FCSTD DOCUMENT  (FreeCAD 0.19R19405 (Git))
Label: Mid_Layer-Tent
License: All rights reserved
LicenseURL: http://en.wikipedia.org/wiki/All_rights_reserved
objects: Sketcher::SketchObject×1
note: 1 computed .brp shape members not serialized (recipe doc carries the construction recipe); baked Part::Feature solids carry a one-line shape summary decoded from their .brp

FEATURE [Sketcher::SketchObject] Sketch016
  sketch-geometry (51):
    g0: Circle CenterX=80.788 CenterY=-116.401 CenterZ=0 NormalX=0 NormalY=0 NormalZ=1 AngleXU=0 Radius=1.75
    g1: Circle CenterX=20.7203 CenterY=-116.401 CenterZ=0 NormalX=0 NormalY=0 NormalZ=1 AngleXU=0 Radius=1.75
    g2: Circle CenterX=141.006 CenterY=-116.404 CenterZ=0 NormalX=0 NormalY=0 NormalZ=1 AngleXU=0 Radius=1.75
    g3: Circle CenterX=150.401 CenterY=-95.6476 CenterZ=0 NormalX=0 NormalY=0 NormalZ=1 AngleXU=0 Radius=3.25
    g4: Circle CenterX=20.5561 CenterY=-65.7042 CenterZ=0 NormalX=0 NormalY=0 NormalZ=1 AngleXU=0 Radius=1.75
    g5: Circle CenterX=140.998 CenterY=-65.6964 CenterZ=0 NormalX=0 NormalY=0 NormalZ=1 AngleXU=0 Radius=1.75
    g6: Circle CenterX=150.401 CenterY=-35.6697 CenterZ=0 NormalX=0 NormalY=0 NormalZ=1 AngleXU=0 Radius=3.25
    g7: Circle CenterX=20.3207 CenterY=-14.9935 CenterZ=0 NormalX=0 NormalY=0 NormalZ=1 AngleXU=0 Radius=1.75
    g8: Circle CenterX=141.013 CenterY=-14.9255 CenterZ=0 NormalX=0 NormalY=0 NormalZ=1 AngleXU=0 Radius=1.75
    g9: Circle CenterX=79.4493 CenterY=-8.03912 CenterZ=0 NormalX=0 NormalY=0 NormalZ=1 AngleXU=0 Radius=1.75
    g10: Circle CenterX=105.449 CenterY=-8.03912 CenterZ=0 NormalX=0 NormalY=0 NormalZ=1 AngleXU=0 Radius=1.75
    g11: LineSegment StartX=34.3805 StartY=-12.0047 StartZ=0 EndX=20.5805 EndY=-12.0047 EndZ=0
    g12: LineSegment StartX=34.3805 StartY=-12.0047 StartZ=0 EndX=34.3805 EndY=-18.1547 EndZ=0
    g13: LineSegment StartX=17.3206 StartY=-15.0015 StartZ=0 EndX=17.3206 EndY=-23.1215 EndZ=0
    g14: LineSegment StartX=34.3805 StartY=-18.1547 StartZ=0 EndX=23.4606 EndY=-18.1547 EndZ=0
    g15: LineSegment StartX=23.4606 StartY=-18.1547 StartZ=0 EndX=23.4606 EndY=-113.255 EndZ=0
    g16: LineSegment StartX=17.3987 StartY=-48.1369 StartZ=0 EndX=17.3987 EndY=-82.9869 EndZ=0
    g17: LineSegment StartX=17.7203 StartY=-108.28 StartZ=0 EndX=17.7203 EndY=-116.42 EndZ=0
    g18: LineSegment StartX=20.7013 StartY=-119.401 StartZ=0 EndX=141.151 EndY=-119.401 EndZ=0
    g19: LineSegment StartX=137.861 StartY=-113.251 StartZ=0 EndX=23.711 EndY=-113.251 EndZ=0
    g20: LineSegment StartX=137.861 StartY=-113.251 StartZ=0 EndX=137.861 EndY=-18.151 EndZ=0
    g21: LineSegment StartX=138.084 StartY=-18.151 StartZ=0 EndX=127.164 EndY=-18.151 EndZ=0
    g22: LineSegment StartX=127.211 StartY=-11.999 StartZ=0 EndX=127.211 EndY=-18.149 EndZ=0
    g23: LineSegment StartX=140.999 StartY=-11.9255 StartZ=0 EndX=127.199 EndY=-11.9255 EndZ=0
    g24: ArcOfCircle CenterX=20.3207 CenterY=-14.9935 CenterZ=0 NormalX=0 NormalY=0 NormalZ=1 AngleXU=0 Radius=3.00006 StartAngle=1.48407 EndAngle=3.14425
    g25: ArcOfCircle CenterX=20.7203 CenterY=-116.401 CenterZ=0 NormalX=0 NormalY=0 NormalZ=1 AngleXU=0 Radius=3.00006 StartAngle=3.14791 EndAngle=4.70607
    g26: ArcOfCircle CenterX=141.006 CenterY=-116.404 CenterZ=0 NormalX=0 NormalY=0 NormalZ=1 AngleXU=0 Radius=3.00006 StartAngle=4.76072 EndAngle=6.28982
    g27: ArcOfCircle CenterX=11.3242 CenterY=-22.9139 CenterZ=0 NormalX=0 NormalY=0 NormalZ=1 AngleXU=0 Radius=6 StartAngle=4.71644 EndAngle=6.24858
    g28: ArcOfCircle CenterX=11.3615 CenterY=-35.5431 CenterZ=0 NormalX=0 NormalY=0 NormalZ=1 AngleXU=0 Radius=6.62923 StartAngle=1.57276 EndAngle=4.71435
    g29: ArcOfCircle CenterX=11.3988 CenterY=-48.1722 CenterZ=0 NormalX=0 NormalY=0 NormalZ=1 AngleXU=0 Radius=6 StartAngle=0.00589337 EndAngle=1.57485
    g30: ArcOfCircle CenterX=141.013 CenterY=-14.9255 CenterZ=0 NormalX=0 NormalY=0 NormalZ=1 AngleXU=0 Radius=3.00006 StartAngle=6.24933 EndAngle=7.85859
    g31: LineSegment StartX=144.01 StartY=-108.261 StartZ=0 EndX=144.01 EndY=-116.401 EndZ=0
    g32: LineSegment StartX=144.814 StartY=-83.1385 StartZ=0 EndX=144.814 EndY=-48.2885 EndZ=0
    g33: LineSegment StartX=144.012 StartY=-23.12 StartZ=0 EndX=144.012 EndY=-15 EndZ=0
    g34: Circle CenterX=11.5597 CenterY=-95.5807 CenterZ=0 NormalX=0 NormalY=0 NormalZ=1 AngleXU=0 Radius=3.25
    g35: Circle CenterX=11.3615 CenterY=-35.5431 CenterZ=0 NormalX=0 NormalY=0 NormalZ=1 AngleXU=0 Radius=3.25
    g36: LineSegment StartX=76.1977 StartY=-5.03912 StartZ=0 EndX=108.263 EndY=-5.03912 EndZ=0
    g37: LineSegment StartX=108.303 StartY=-11.0391 StartZ=0 EndX=76.2376 EndY=-11.0391 EndZ=0
    g38: LineSegment StartX=75.4493 StartY=-10.0943 StartZ=0 EndX=75.4493 EndY=-5.76363 EndZ=0
    g39: LineSegment StartX=109.449 StartY=-10.0255 StartZ=0 EndX=109.449 EndY=-5.69488 EndZ=0
    g40: ArcOfCircle CenterX=76.4173 CenterY=-6.01471 CenterZ=0 NormalX=0 NormalY=0 NormalZ=1 AngleXU=0 Radius=1 StartAngle=1.79221 EndAngle=2.8878
    g41: ArcOfCircle CenterX=76.4488 CenterY=-10.0617 CenterZ=0 NormalX=0 NormalY=0 NormalZ=1 AngleXU=0 Radius=1 StartAngle=3.17423 EndAngle=4.4996
    g42: ArcOfCircle CenterX=108.5 CenterY=-6.01046 CenterZ=0 NormalX=0 NormalY=0 NormalZ=1 AngleXU=0 Radius=1 StartAngle=0.321062 EndAngle=1.81081
    g43: ArcOfCircle CenterX=108.45 CenterY=-10.05 CenterZ=0 NormalX=0 NormalY=0 NormalZ=1 AngleXU=0 Radius=1 StartAngle=4.56487 EndAngle=6.30762
    g44: ArcOfCircle CenterX=11.3988 CenterY=-82.9522 CenterZ=0 NormalX=0 NormalY=0 NormalZ=1 AngleXU=0 Radius=6 StartAngle=4.74889 EndAngle=6.27741
    g45: ArcOfCircle CenterX=11.5597 CenterY=-95.5807 CenterZ=0 NormalX=0 NormalY=0 NormalZ=1 AngleXU=0 Radius=6.63272 StartAngle=1.56205 EndAngle=4.70364
    g46: ArcOfCircle CenterX=11.7207 CenterY=-108.209 CenterZ=0 NormalX=0 NormalY=0 NormalZ=1 AngleXU=0 Radius=6 StartAngle=6.27138 EndAngle=7.89048
    g47: ArcOfCircle CenterX=150 CenterY=-22.9967 CenterZ=0 NormalX=0 NormalY=0 NormalZ=1 AngleXU=0 Radius=5.98868 StartAngle=3.16219 EndAngle=4.74658
    g48: ArcOfCircle CenterX=150.401 CenterY=-35.6697 CenterZ=0 NormalX=0 NormalY=0 NormalZ=1 AngleXU=0 Radius=6.69074 StartAngle=4.74177 EndAngle=7.88336
    g49: ArcOfCircle CenterX=150.802 CenterY=-48.3428 CenterZ=0 NormalX=0 NormalY=0 NormalZ=1 AngleXU=0 Radius=5.98868 StartAngle=1.60498 EndAngle=3.13253
    g50: LineSegment [constr] StartX=17.3987 StartY=-65.5619 StartZ=0 EndX=11.4606 EndY=-65.5619 EndZ=0
  constraints (113):
    c: DistanceX(g11,g11) = 13.8
    c: DistanceY(g12,g12) = 6.15
    c: DistanceY(g15,g15) = 95.1
    c: DistanceY(g13,g13) = 8.12
    c: DistanceY(g16,g16) = 34.85
    c: DistanceY(g17,g17) = 8.14
    c: DistanceX(g18,g18) = 120.45
    c: DistanceX(g19,g19) = 114.15
    c: Coincident(g11,g24)
    c: Coincident(g13,g24)
    c: Horizontal(g11)
    c: Vertical(g13)
    c: Vertical(g12)
    c: Vertical(g20)
    c: Vertical(g22)
    c: Vertical(g15)
    c: Vertical(g16)
    c: Vertical(g17)
    c: Horizontal(g19)
    c: Horizontal(g18)
    c: Horizontal(g14)
    c: Horizontal(g21)
    c: Horizontal(g23)
    c: Coincident(g25,g17)
    c: Coincident(g18,g25)
    c: Coincident(g26,g18)
    c: Coincident(g29,g16)
    c: Coincident(g30,g23)
    c: Radius(g27) = 6
    c: Coincident(g29,g28)
    c: Coincident(g27,g28)
    c: Coincident(g27,g13)
    c: Vertical(g31)
    c: Vertical(g32)
    c: Vertical(g33)
    c: Horizontal(g36)
    c: Horizontal(g37)
    c: Vertical(g38)
    c: Vertical(g39)
    c: Equal(g37,g36)
    c: Equal(g38,g39)
    c: DistanceY(g9,g36) = 3
    c: DistanceX(g38,g9) = 4
    c: DistanceY(g10,g36) = 3
    c: DistanceX(g10,g39) = 4
    c: Coincident(g7,g24)
    c: Equal(g8,g10)
    c: Equal(g10,g9)
    c: Equal(g9,g7)
    c: Equal(g7,g4)
    c: Equal(g4,g1)
    c: Equal(g1,g0)
    c: Equal(g0,g2)
    c: Equal(g2,g5)
    c: Diameter(g7) = 3.5
    c: Equal(g34,g35)
    c: Equal(g35,g3)
    c: Equal(g3,g6)
    c: Coincident(g1,g25)
    c: Coincident(g2,g26)
    c: Coincident(g8,g30)
    c: Coincident(g40,g36)
    c: Coincident(g40,g38)
    c: Radius(g40) = 1
    c: Coincident(g41,g37)
    c: Coincident(g41,g38)
    c: Coincident(g42,g36)
    c: Coincident(g42,g39)
    c: Coincident(g43,g39)
    c: Coincident(g43,g37)
    c: Equal(g40,g41)
    c: Equal(g41,g43)
    c: Equal(g43,g42)
    c: DistanceX(g38,g39) = 34
    c: DistanceY(g37,g36) = 6
    c: Coincident(g28,g35)
    c: Symmetric(g28,g27,g28)
    c: Symmetric(g29,g27,g28)
    c: DistanceX(g13,g14) = 6.14
    c: Coincident(g15,g14)
    c: Coincident(g12,g14)
    c: Coincident(g12,g11)
    c: Equal(g27,g44) = 6
    c: Coincident(g46,g45)
    c: Coincident(g44,g45)
    c: Symmetric(g45,g44,g45)
    c: Symmetric(g46,g44,g45)
    c: Coincident(g16,g44)
    c: Coincident(g46,g17)
    c: DistanceY(g18,g1) = 3
    c: DistanceX(g17,g1) = 3
    c: Coincident(g47,g33)
    c: Coincident(g48,g6)
    c: Coincident(g48,g47)
    c: Coincident(g49,g48)
    c: Coincident(g49,g32)
    c: Symmetric(g47,g48,g6)
    c: Symmetric(g47,g49,g6)
    c: Symmetric(g16,g16,g50)
    c: Horizontal(g50)
    c: Symmetric(g28,g34,g50)
    c: DistanceX(g50,g14) = 12
    c: Equal(g15,g20)
    c: Equal(g14,g21)
    c: Equal(g22,g12)
    c: Equal(g11,g23)
    c: Equal(g13,g33)
    c: Equal(g17,g31)
    c: Equal(g32,g16)
    c: Diameter(g35) = 6.5
    c: Equal(g24,g25)
    c: Equal(g25,g26)
    c: Equal(g26,g30)
